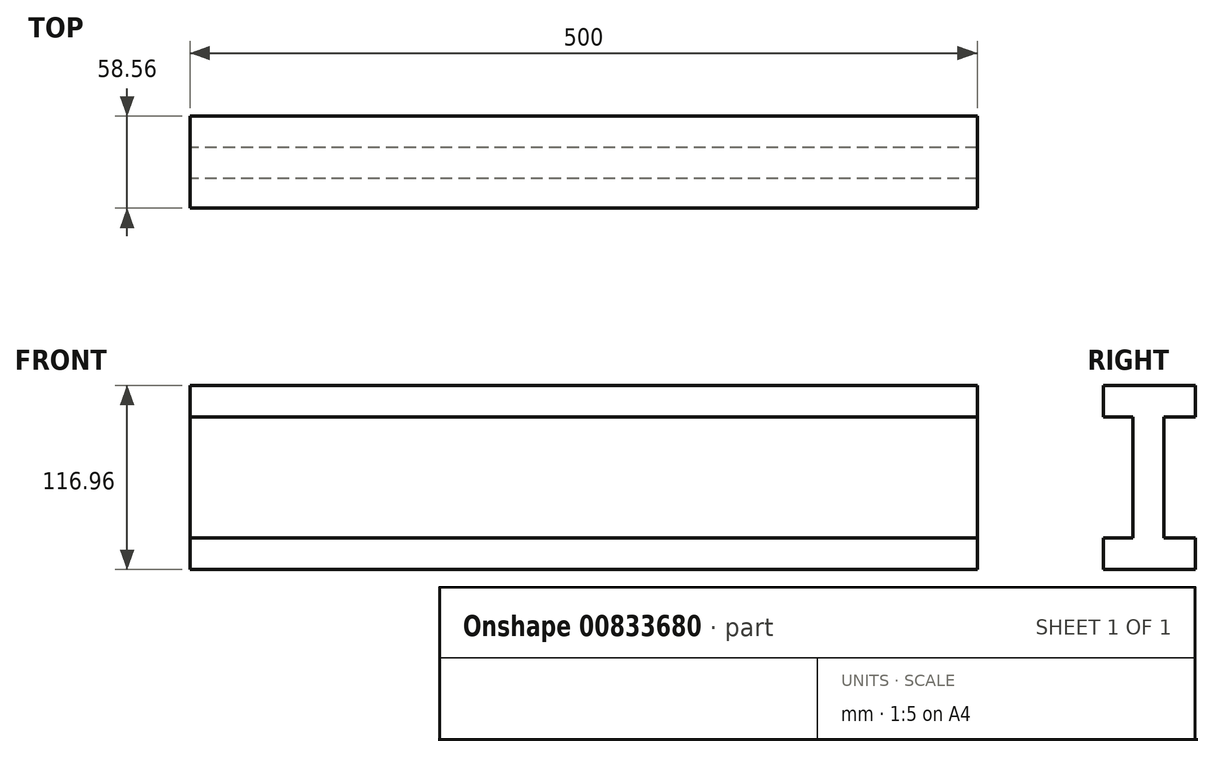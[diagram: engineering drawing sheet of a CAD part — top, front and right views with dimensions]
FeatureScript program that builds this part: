
annotation { "Feature Type Name" : "Feature", "Feature Type Description" : "" }
export const myFeature = defineFeature(function(context is Context, id is Id, definition is map)
    precondition{}
    {
        {
            var Q0;
            Q0=qCreatedBy(makeId("Right.planeOp"),FACE);
            var sketch = newSketch(context, id + "F0", { "sketchPlane" : qUnion([Q0])});
            skLineSegment(sketch, "E0.left", {"start": v(-11.02, 0) * mm, "end": v(-11.02, 38.45) * mm});
            skLineSegment(sketch, "E0.right", {"start": v(8.7, 0) * mm, "end": v(8.7, 38.45) * mm});
            skLineSegment(sketch, "E1.bottom", {"start": v(-29.82, 38.45) * mm, "end": v(-11.02, 38.45) * mm});
            skLineSegment(sketch, "E1.top", {"start": v(-29.82, 58.48) * mm, "end": v(28.74, 58.48) * mm});
            skLineSegment(sketch, "E1.left", {"start": v(-29.82, 38.45) * mm, "end": v(-29.82, 58.48) * mm});
            skLineSegment(sketch, "E1.right", {"start": v(28.74, 38.45) * mm, "end": v(28.74, 58.48) * mm});
            skLineSegment(sketch, "E2.MirrorCS", {"start": v(-29.82, -38.45) * mm, "end": v(-29.82, -58.48) * mm});
            skLineSegment(sketch, "E3.MirrorCS", {"start": v(-29.82, -58.48) * mm, "end": v(28.74, -58.48) * mm});
            skLineSegment(sketch, "E4.MirrorCS", {"start": v(28.74, -38.45) * mm, "end": v(28.74, -58.48) * mm});
            skLineSegment(sketch, "E5.MirrorCS", {"start": v(8.7, 0) * mm, "end": v(8.7, -38.45) * mm});
            skLineSegment(sketch, "E6.MirrorCS", {"start": v(-11.02, 0) * mm, "end": v(-11.02, -38.45) * mm});
            skLineSegment(sketch, "E7.MirrorCS", {"start": v(-29.82, -38.45) * mm, "end": v(-11.02, -38.45) * mm});
            skLineSegment(sketch, "E8.trimOffspring", {"start": v(8.7, 38.45) * mm, "end": v(28.74, 38.45) * mm});
            skLineSegment(sketch, "E9.trimOffspring", {"start": v(8.7, -38.45) * mm, "end": v(28.74, -38.45) * mm});
            skSolve(sketch);
        }
        {
            var Q0;
            Q0=makeQuery(id+"F0.imprint","IMPRINT",FACE,{"disambiguationData":[TD([[makeQuery(id+"F0.imprint","IMPRINT",EDGE,{"derivedFrom":sQuery(id+"F0.wireOp",EDGE,"E0.left")}),-1.0]])]});
            extrude(context, id + "F1", {"entities" : qUnion([Q0]), "depth" : 500 * mm, "offsetDistance" : 25 * mm});
        }
    });
